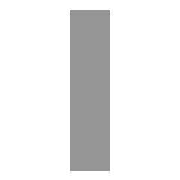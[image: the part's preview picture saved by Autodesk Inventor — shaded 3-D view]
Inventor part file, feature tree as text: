
AUTODESK INVENTOR PART (.ipt)
format: ipt  version: 2019.4 (Build 234330000, 330)  size: 116,736 bytes
history: native  units: mm (DEFAULTED — no unit token found)
features: other x4, plane x3, split x2, sketch x2
ambient origin geometry x8: Origin, YZ Plane, XZ Plane, XY Plane, X Axis, Y Axis, Z Axis, Center Point
bodies: Solid1 (feature_tree), Body (feature_tree)
feature tree (11):
  parser-record x1  (decoder bookkeeping rows leaked as tree rows — omitted from the tree; the rows remain in map.json)
  other  "Driven Length"
  other  "Start plane"
  other  "End plane"
  plane  "Work Plane7"
  split  "Split4"
  plane  "Work Plane8"
  split  "Split5"
  sketch  "Sketch3"  dims[d0=12.7mm]
  plane  "Work Plane3"
  sketch  "Sketch4"  dims[d1=9.525mm d2=471.380039mm d3=0.0mm d4=4.7625mm d5=6.35mm d6=-7.850112mm d7=463.529927mm d8=90.0deg d9=471.380039mm]
